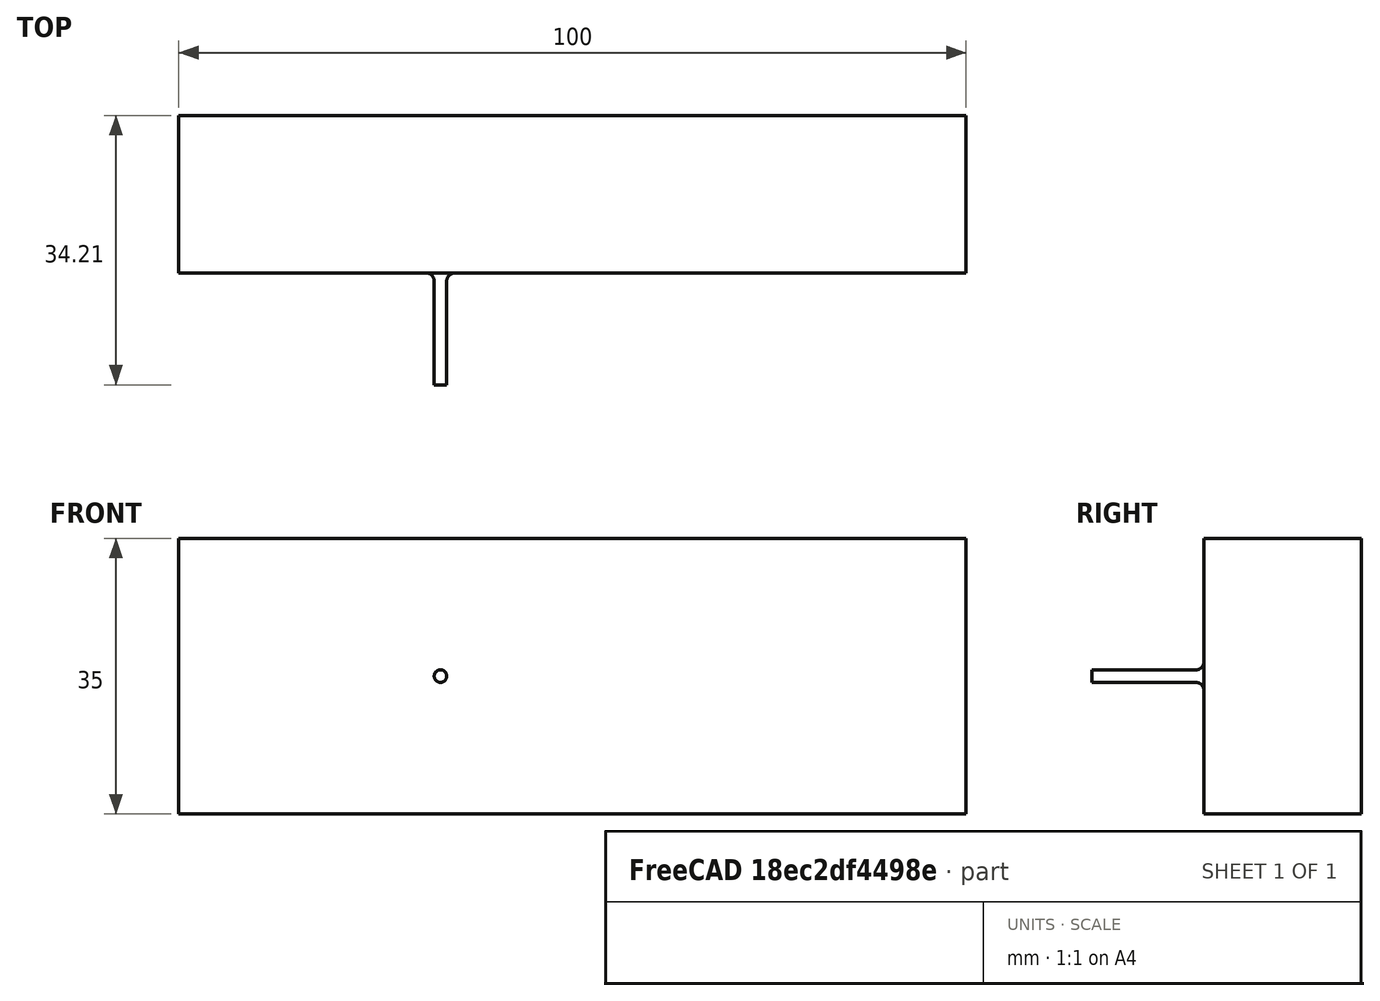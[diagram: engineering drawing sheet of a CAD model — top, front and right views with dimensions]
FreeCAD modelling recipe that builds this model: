
FCSTD DOCUMENT  (FreeCAD 0.20R29603 (Git))
Label: actii_fillet
License: All rights reserved
LicenseURL: http://en.wikipedia.org/wiki/All_rights_reserved
objects: Part::Cylinder×1, Part::Box×1, Part::MultiFuse×1, Part::Fillet×1
note: 4 computed .brp shape members not serialized (recipe doc carries the construction recipe); baked Part::Feature solids carry a one-line shape summary decoded from their .brp

FEATURE [Part::Cylinder] Cylinder001  label="UpstreamInjector"
  Angle = 360
  AttacherType = Attacher::AttachEngine3D
  FirstAngle = 0
  Height = 15
  Placement = pos=(533.235,-7.5295,0) rot=(1,0,0;1.5708rad)
  Radius = 0.795
  SecondAngle = 0
  expr: .Placement.Base.x = 383.28 + 223 - 72.25 - 0.795
  expr: .Placement.Base.y = -8.3245 + 1.59 / 2
FEATURE [Part::Box] Box  label="Cube"
  AttacherType = Attacher::AttachEngine3D
  Height = 35
  Length = 100
  Placement = pos=(500,-8.3245,-17.5) rot=(0,0,1;0rad)
  Width = 20
FEATURE [Part::MultiFuse] Fusion
  Shapes = -> [Cylinder001,Box]
FEATURE [Part::Fillet] Fillet
  Base = -> Fusion
  Edges = 1 edges r=1: [Edge1]
